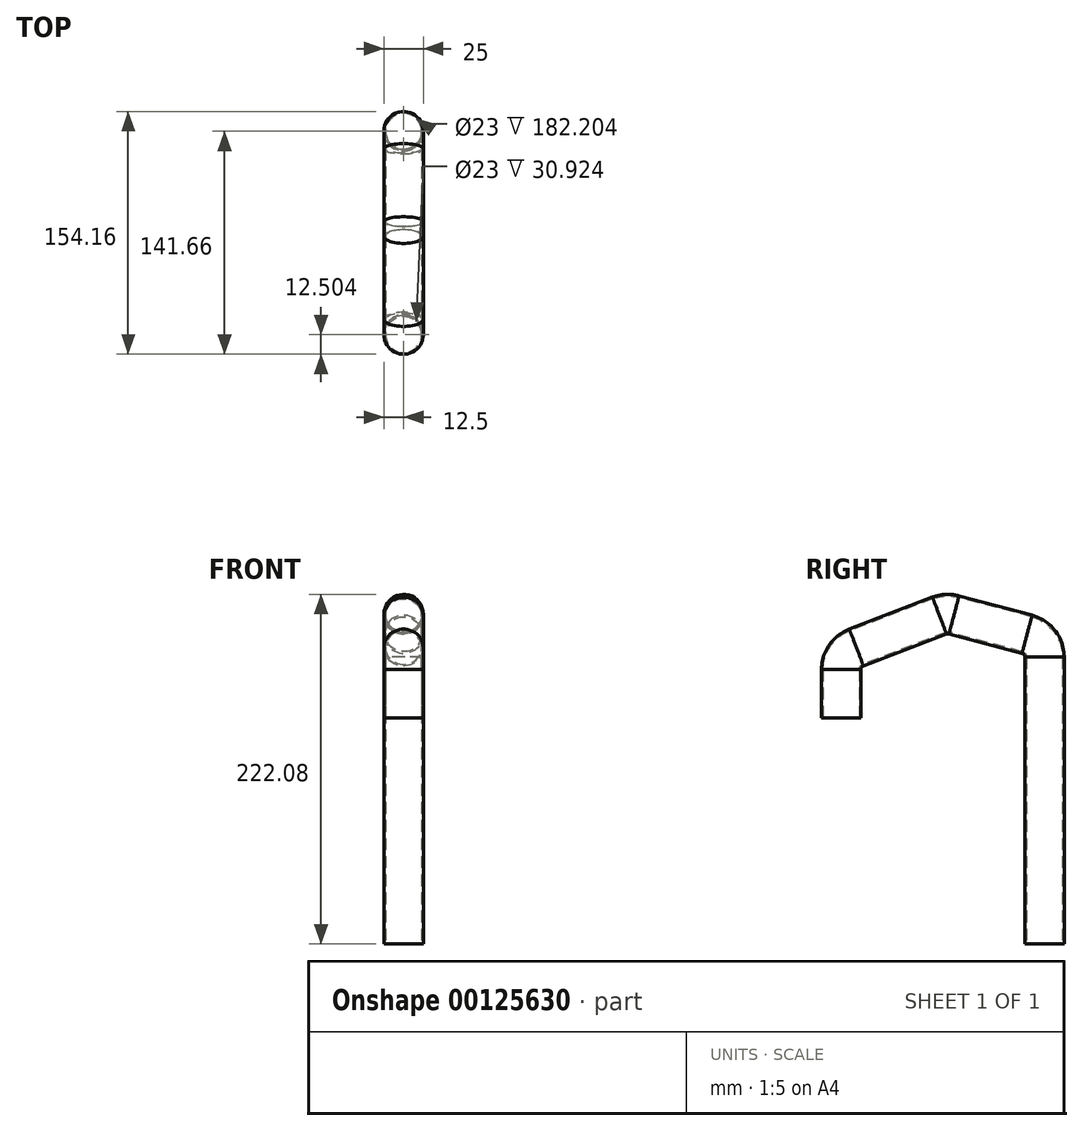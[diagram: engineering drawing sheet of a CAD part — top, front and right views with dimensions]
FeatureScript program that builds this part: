
annotation { "Feature Type Name" : "Feature", "Feature Type Description" : "" }
export const myFeature = defineFeature(function(context is Context, id is Id, definition is map)
    precondition{}
    {
        {
            var Q0;
            Q0=qCreatedBy(makeId("Top.planeOp"),FACE);
            var sketch = newSketch(context, id + "F0", { "sketchPlane" : qUnion([Q0])});
            skCircle(sketch, "E0", {"center": v(0, 0) * mm, "radius": 12.5 * mm});
            skSolve(sketch);
        }
        {
            var Q0;
            Q0=makeQuery(id+"F0.imprint","IMPRINT",FACE,{"disambiguationData":[TD([[makeQuery(id+"F0.imprint","IMPRINT",EDGE,{"derivedFrom":sQuery(id+"F0.wireOp",EDGE,"E0")}),1.0]])]});
            extrude(context, id + "F1", {"entities" : qUnion([Q0]), "depth" : 100 * mm});
        }
        {
            var Q0;
            Q0=makeQuery(id+"F1.opExtrude","CAP_FACE",FACE,{"disambiguationData":[OSD([sQuery(id+"F0.wireOp",EDGE,"E0")])],"isStart":false});
            var Q1;
            Q1=makeQuery(id+"F1.opExtrude","CAP_FACE",FACE,{"disambiguationData":[OSD([sQuery(id+"F0.wireOp",EDGE,"E0")])],"isStart":true});
            shell(context, id + "F2", {"entities" : qUnion([Q0, Q1]), "thickness" : 1 * mm});
        }
        {
            var Q0;
            Q0=qCreatedBy(makeId("Right.planeOp"),FACE);
            var sketch = newSketch(context, id + "F3", { "sketchPlane" : qUnion([Q0])});
            skLineSegment(sketch, "E1", {"start": v(0, 100.08) * mm, "end": v(0, 182.28) * mm});
            skLineSegment(sketch, "E2", {"start": v(-11.16, 196.78) * mm, "end": v(-57.57, 209.08) * mm});
            skLineSegment(sketch, "E3", {"start": v(-66.8, 208.58) * mm, "end": v(-119.54, 188.29) * mm});
            skLineSegment(sketch, "E4", {"start": v(-129.16, 174.29) * mm, "end": v(-129.16, 143.36) * mm});
            skPoint(sketch, "E5.visualSharp", {"position": v(-129.16, 184.6) * mm});
            skArc(sketch, "E5.filletArc", {"start": v(-119.54, 188.29) * mm, "mid": v(-126.52, 182.78) * mm, "end": v(-129.16, 174.29) * mm});
            skPoint(sketch, "E6.visualSharp", {"position": v(-62.26, 210.32) * mm});
            skArc(sketch, "E6.filletArc", {"start": v(-57.57, 209.08) * mm, "mid": v(-62.22, 209.55) * mm, "end": v(-66.8, 208.58) * mm});
            skPoint(sketch, "E7.visualSharp", {"position": v(0, 193.83) * mm});
            skArc(sketch, "E7.filletArc", {"start": v(0, 182.28) * mm, "mid": v(-3.11, 191.43) * mm, "end": v(-11.16, 196.78) * mm});
            skSolve(sketch);
        }
        {
            var Q0;
            Q0=makeQuery(id+"F1.opExtrude","CAP_FACE",FACE,{"disambiguationData":[OSD([sQuery(id+"F0.wireOp",EDGE,"E0")])],"isStart":false});
            var Q1;
            Q1=sQuery(id+"F3.wireOp",EDGE,"E1");
            var Q2;
            Q2=sQuery(id+"F3.wireOp",EDGE,"E7.filletArc");
            var Q3;
            Q3=sQuery(id+"F3.wireOp",EDGE,"E2");
            var Q4;
            Q4=sQuery(id+"F3.wireOp",EDGE,"E6.filletArc");
            var Q5;
            Q5=sQuery(id+"F3.wireOp",EDGE,"E3");
            var Q6;
            Q6=sQuery(id+"F3.wireOp",EDGE,"E5.filletArc");
            var Q7;
            Q7=sQuery(id+"F3.wireOp",EDGE,"E4");
            sweep(context, id + "F4", {"operationType" : NewBodyOperationType.ADD, "profiles" : qUnion([Q0]), "path" : qUnion([Q1, Q2, Q3, Q4, Q5, Q6, Q7])});
        }
    });
